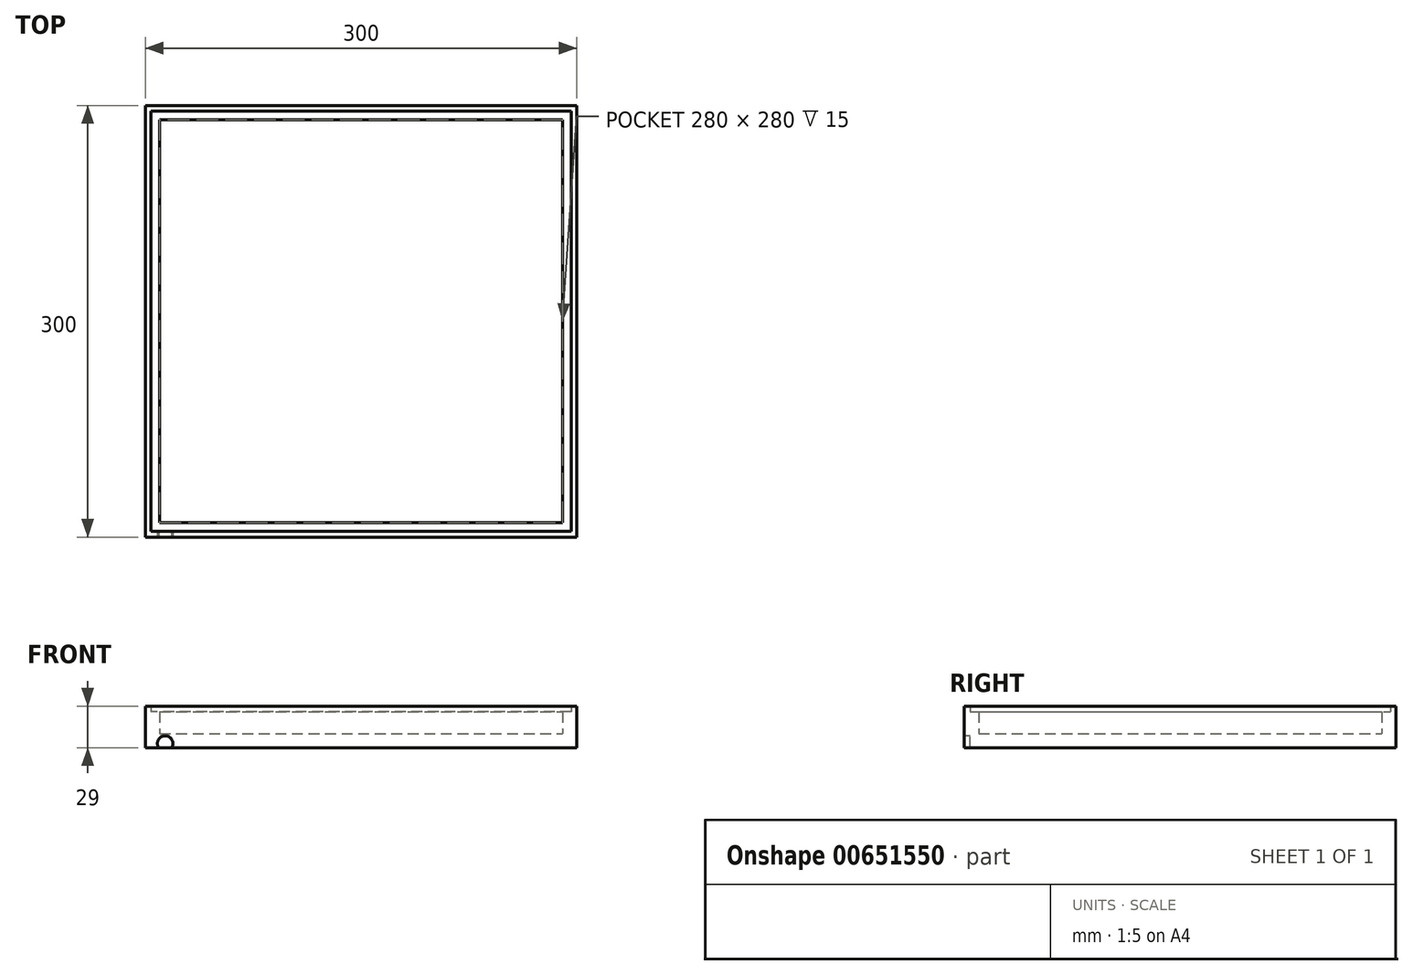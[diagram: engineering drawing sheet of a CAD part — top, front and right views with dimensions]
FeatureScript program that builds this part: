
annotation { "Feature Type Name" : "Feature", "Feature Type Description" : "" }
export const myFeature = defineFeature(function(context is Context, id is Id, definition is map)
    precondition{}
    {
        {
            var Q0;
            Q0=qCreatedBy(makeId("Top.planeOp"),FACE);
            var sketch = newSketch(context, id + "F0", { "sketchPlane" : qUnion([Q0])});
            skLineSegment(sketch, "E0.bottom", {"start": v(-54.47, -60.65) * mm, "end": v(245.53, -60.65) * mm});
            skLineSegment(sketch, "E0.top", {"start": v(-54.47, 239.35) * mm, "end": v(245.53, 239.35) * mm});
            skLineSegment(sketch, "E0.left", {"start": v(-54.47, -60.65) * mm, "end": v(-54.47, 239.35) * mm});
            skLineSegment(sketch, "E0.right", {"start": v(245.53, -60.65) * mm, "end": v(245.53, 239.35) * mm});
            skSolve(sketch);
        }
        {
            var Q0;
            Q0=makeQuery(id+"F0.imprint","IMPRINT",FACE,{"disambiguationData":[TD([[makeQuery(id+"F0.imprint","IMPRINT",EDGE,{"derivedFrom":sQuery(id+"F0.wireOp",EDGE,"E0.bottom")}),1.0]])]});
            extrude(context, id + "F1", {"entities" : qUnion([Q0]), "depth" : 25 * mm, "offsetDistance" : 25 * mm});
        }
        {
            var Q0;
            Q0=makeQuery(id+"F1.opExtrude","SWEPT_FACE",FACE,{"disambiguationData":[OSD([sQuery(id+"F0.wireOp",EDGE,"E0.bottom")])]});
            var sketch = newSketch(context, id + "F2", { "sketchPlane" : qUnion([Q0])});
            skCircle(sketch, "E1", {"center": v(-40.62, 3) * mm, "radius": 5.4 * mm});
            skSolve(sketch);
        }
        {
            var Q0;
            Q0=makeQuery(id+"F1.opExtrude","CAP_FACE",FACE,{"disambiguationData":[OSD([sQuery(id+"F0.wireOp",EDGE,"E0.bottom"),sQuery(id+"F0.wireOp",EDGE,"E0.top"),sQuery(id+"F0.wireOp",EDGE,"E0.left"),sQuery(id+"F0.wireOp",EDGE,"E0.right")])],"isStart":false});
            shell(context, id + "F3", {"entities" : qUnion([Q0]), "thickness" : 10 * mm});
        }
        {
            var Q0;
            {var subQ0=sQuery(id+"F2.wireOp",EDGE,"E1");var subQ1=makeQuery(id+"F1.opExtrude","CAP_EDGE",EDGE,{"disambiguationData":[OSD([sQuery(id+"F0.wireOp",EDGE,"E0.bottom")])],"isStart":true});var subQ2=makeQuery(id+"F2.imprint","INTERSECT",VERTEX,{"disambiguationData":[OD(0.0)],"derivedFrom":[subQ1,subQ0]});Q0=makeQuery(id+"F2.imprint","IMPRINT",FACE,{"disambiguationData":[TD([[makeQuery(id+"F2.imprint","IMPRINT",EDGE,{"disambiguationData":[TD([[subQ2,1.0]])],"derivedFrom":subQ0}),1.0]])]});}
            extrude(context, id + "F4", {"entities" : qUnion([Q0]), "operationType" : NewBodyOperationType.REMOVE, "oppositeDirection" : true, "depth" : 4 * mm, "offsetDistance" : 25 * mm});
        }
        {
            var Q0;
            Q0=makeQuery(id+"F1.opExtrude","CAP_FACE",FACE,{"disambiguationData":[OSD([sQuery(id+"F0.wireOp",EDGE,"E0.bottom"),sQuery(id+"F0.wireOp",EDGE,"E0.top"),sQuery(id+"F0.wireOp",EDGE,"E0.left"),sQuery(id+"F0.wireOp",EDGE,"E0.right")])],"isStart":false});
            var sketch = newSketch(context, id + "F5", { "sketchPlane" : qUnion([Q0])});
            skLineSegment(sketch, "E2.bottom", {"start": v(241.53, -56.65) * mm, "end": v(-50.47, -56.65) * mm});
            skLineSegment(sketch, "E2.top", {"start": v(241.53, 235.35) * mm, "end": v(-50.47, 235.35) * mm});
            skLineSegment(sketch, "E2.left", {"start": v(241.53, -56.65) * mm, "end": v(241.53, 235.35) * mm});
            skLineSegment(sketch, "E2.right", {"start": v(-50.47, -56.65) * mm, "end": v(-50.47, 235.35) * mm});
            skSolve(sketch);
        }
        {
            var Q0;
            Q0=makeQuery(id+"F5.imprint","IMPRINT",FACE,{"disambiguationData":[TD([[makeQuery(id+"F5.imprint","IMPRINT",EDGE,{"derivedFrom":sQuery(id+"F5.wireOp",EDGE,"E2.bottom")}),1.0]])]});
            extrude(context, id + "F6", {"entities" : qUnion([Q0]), "operationType" : NewBodyOperationType.ADD, "depth" : 4 * mm, "offsetDistance" : 25 * mm});
        }
    });
